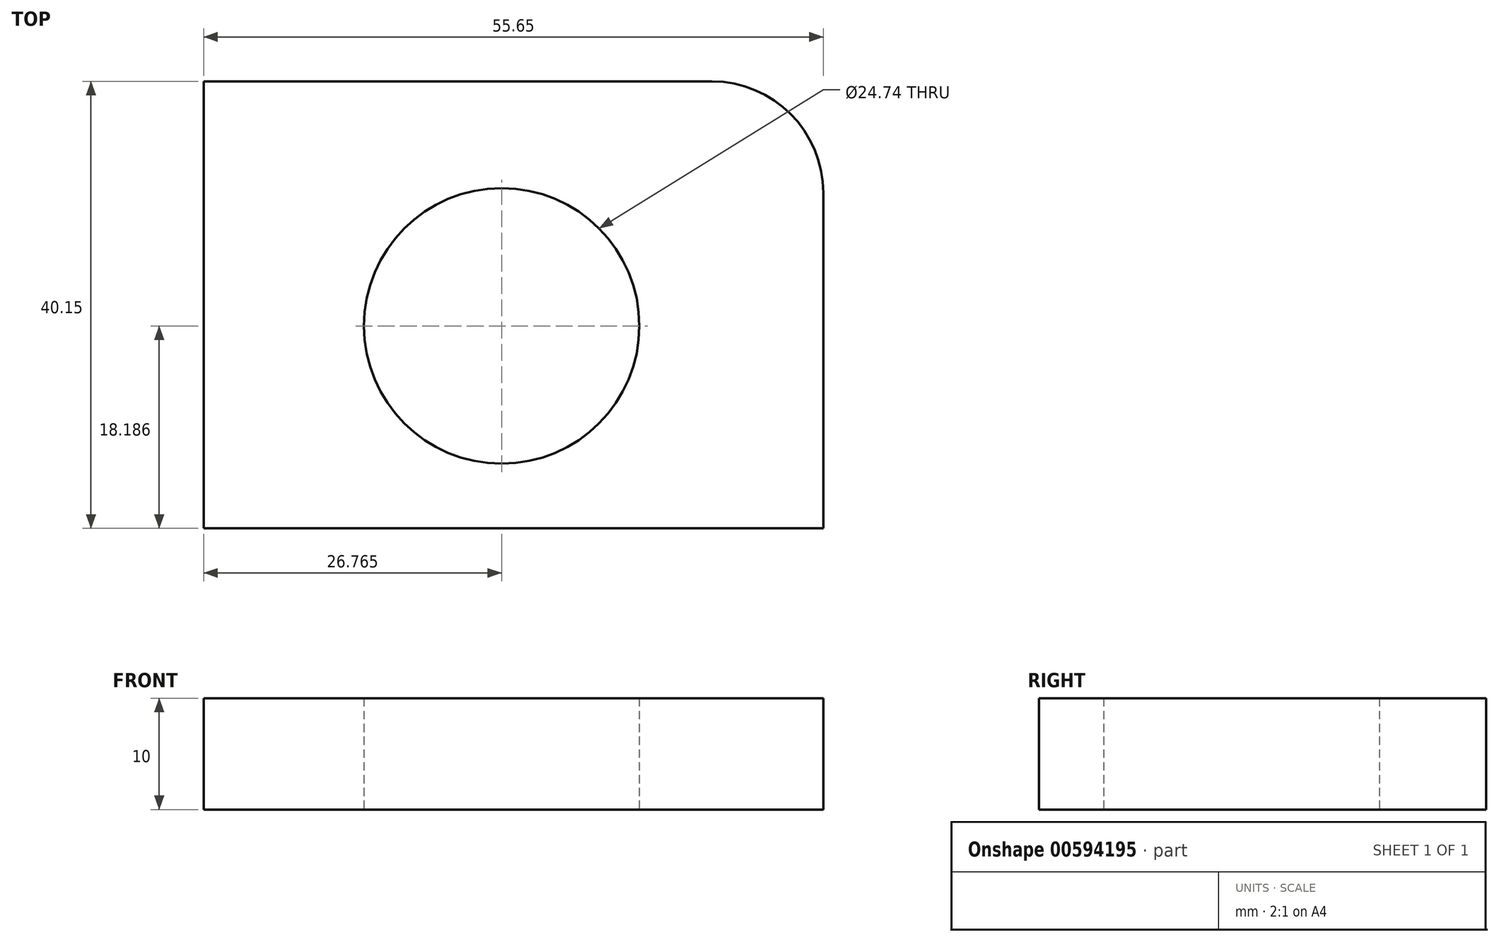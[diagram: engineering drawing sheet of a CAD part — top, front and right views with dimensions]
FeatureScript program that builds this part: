
annotation { "Feature Type Name" : "Feature", "Feature Type Description" : "" }
export const myFeature = defineFeature(function(context is Context, id is Id, definition is map)
    precondition{}
    {
        {
            var Q0;
            Q0=qCreatedBy(makeId("Top.planeOp"),FACE);
            var sketch = newSketch(context, id + "F0", { "sketchPlane" : qUnion([Q0])});
            skLineSegment(sketch, "E0.bottom", {"start": v(0, 0) * mm, "end": v(55.65, 0) * mm});
            skLineSegment(sketch, "E0.top", {"start": v(0, 40.15) * mm, "end": v(45.65, 40.15) * mm});
            skLineSegment(sketch, "E0.left", {"start": v(0, 0) * mm, "end": v(0, 40.15) * mm});
            skLineSegment(sketch, "E0.right", {"start": v(55.65, 0) * mm, "end": v(55.65, 30.15) * mm});
            skPoint(sketch, "E1.visualSharp", {"position": v(55.65, 40.15) * mm});
            skArc(sketch, "E1.filletArc", {"start": v(55.65, 30.15) * mm, "mid": v(52.72, 37.22) * mm, "end": v(45.65, 40.15) * mm});
            skCircle(sketch, "E2", {"center": v(26.77, 18.19) * mm, "radius": 12.37 * mm});
            skSolve(sketch);
        }
        {
            var Q0;
            Q0 = qSketchRegion(id + "F0", true);
            extrude(context, id + "F1", {"entities" : qUnion([Q0]), "depth" : 10 * mm, "offsetDistance" : 25 * mm});
        }
    });
